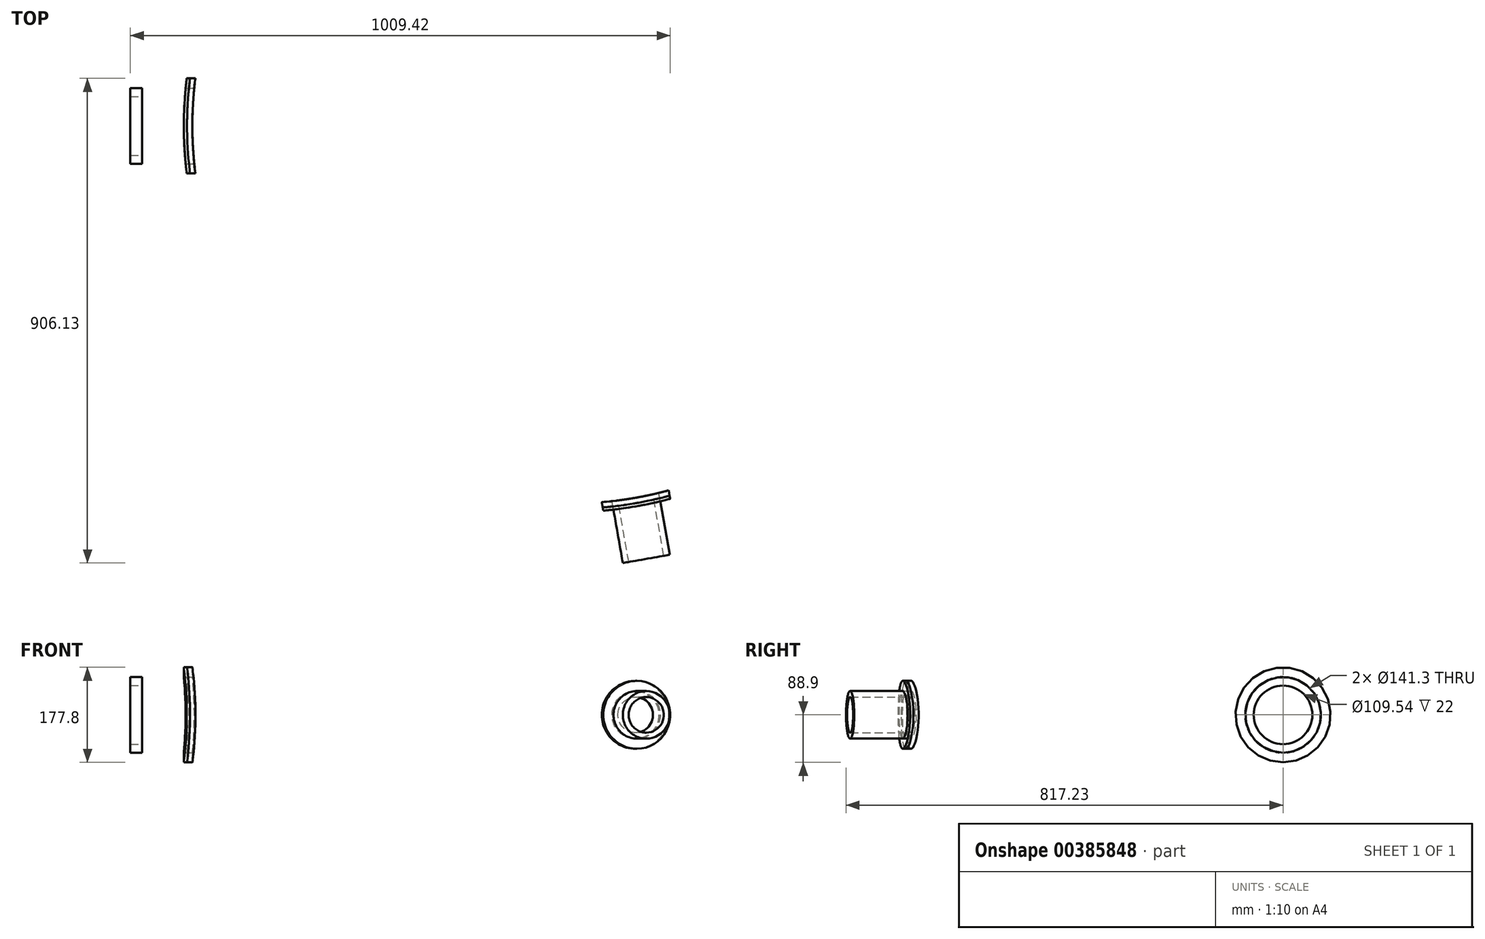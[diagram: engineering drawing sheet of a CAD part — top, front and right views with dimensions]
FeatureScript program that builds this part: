
annotation { "Feature Type Name" : "Feature", "Feature Type Description" : "" }
export const myFeature = defineFeature(function(context is Context, id is Id, definition is map)
    precondition{}
    {
        {
            var Q0;
            Q0=qCreatedBy(makeId("Top.planeOp"),FACE);
            var sketch = newSketch(context, id + "F0", { "sketchPlane" : qUnion([Q0])});
            skArc(sketch, "E0", {"start": v(-5.53, 715.98) * mm, "mid": v(-716, 0) * mm, "end": v(-5.53, -715.98) * mm});
            skArc(sketch, "E1.0", {"start": v(-1.5, 706) * mm, "mid": v(-706, 0) * mm, "end": v(-1.5, -706) * mm});
            skLineSegment(sketch, "E2", {"start": v(0, 716) * mm, "end": v(0, -716) * mm, "construction": true});
            skLineSegment(sketch, "E3", {"start": v(-716, 0) * mm, "end": v(716, 0) * mm, "construction": true});
            skLineSegment(sketch, "E4", {"start": v(1.5, 709) * mm, "end": v(1.5, 706) * mm});
            skCircle(sketch, "E5.0", {"center": v(0, 0) * mm, "radius": 709 * mm, "construction": true});
            skLineSegment(sketch, "E6", {"start": v(1.5, 709) * mm, "end": v(5.53, 715.98) * mm});
            skLineSegment(sketch, "E7.MirrorCS", {"start": v(-1.5, 709) * mm, "end": v(-1.5, 706) * mm});
            skLineSegment(sketch, "E8.MirrorCS", {"start": v(-1.5, 709) * mm, "end": v(-5.53, 715.98) * mm});
            skLineSegment(sketch, "E9.MirrorCS", {"start": v(1.5, -709) * mm, "end": v(1.5, -706) * mm});
            skLineSegment(sketch, "E10.MirrorCS", {"start": v(-1.5, -709) * mm, "end": v(-1.5, -706) * mm});
            skLineSegment(sketch, "E11.MirrorCS", {"start": v(-1.5, -709) * mm, "end": v(-5.53, -715.98) * mm});
            skLineSegment(sketch, "E12.MirrorCS", {"start": v(1.5, -709) * mm, "end": v(5.53, -715.98) * mm});
            skArc(sketch, "E13.trimOffspring", {"start": v(5.53, -715.98) * mm, "mid": v(716, 0) * mm, "end": v(5.53, 715.98) * mm});
            skArc(sketch, "E14.trimOffspring", {"start": v(1.5, -706) * mm, "mid": v(706, 0) * mm, "end": v(1.5, 706) * mm});
            skArc(sketch, "E15.0", {"start": v(-5.58, 721.98) * mm, "mid": v(-722, 0) * mm, "end": v(-5.58, -721.98) * mm});
            skLineSegment(sketch, "E16", {"start": v(-5.58, 721.98) * mm, "end": v(-5.53, 715.98) * mm});
            skLineSegment(sketch, "E17", {"start": v(-5.58, -721.98) * mm, "end": v(-5.53, -715.98) * mm});
            skLineSegment(sketch, "E18.MirrorCS", {"start": v(5.58, 721.98) * mm, "end": v(5.53, 715.98) * mm});
            skArc(sketch, "E19.MirrorCS", {"start": v(5.58, 721.98) * mm, "mid": v(722, 0) * mm, "end": v(5.58, -721.98) * mm});
            skLineSegment(sketch, "E20.MirrorCS", {"start": v(5.58, -721.98) * mm, "end": v(5.53, -715.98) * mm});
            skSolve(sketch);
        }
        {
            var Q0;
            Q0=makeQuery(id+"F0.imprint","IMPRINT",FACE,{"disambiguationData":[TD([[makeQuery(id+"F0.imprint","IMPRINT",EDGE,{"derivedFrom":sQuery(id+"F0.wireOp",EDGE,"E0")}),1.0]])]});
            var Q1;
            Q1=makeQuery(id+"F0.imprint","IMPRINT",FACE,{"disambiguationData":[TD([[makeQuery(id+"F0.imprint","IMPRINT",EDGE,{"derivedFrom":sQuery(id+"F0.wireOp",EDGE,"E4")}),1.0]])]});
            extrude(context, id + "F1", {"entities" : qUnion([Q0, Q1]), "endBound" : BoundingType.SYMMETRIC, "depth" : 1200 * mm});
        }
        {
            var Q0;
            Q0=qCreatedBy(makeId("Right.planeOp"),FACE);
            var sketch = newSketch(context, id + "F2", { "sketchPlane" : qUnion([Q0])});
            skLineSegment(sketch, "E21", {"start": v(0, 612.66) * mm, "end": v(0, -646.3) * mm, "construction": true});
            skLineSegment(sketch, "E22", {"start": v(-709, 600) * mm, "end": v(-726.72, 600) * mm});
            skLineSegment(sketch, "E23", {"start": v(-726.72, 600) * mm, "end": v(-726.72, 589.77) * mm});
            skLineSegment(sketch, "E24", {"start": v(-726.72, 589.77) * mm, "end": v(-709, 600) * mm});
            skLineSegment(sketch, "E25", {"start": v(-747.88, 0) * mm, "end": v(755.94, 0) * mm, "construction": true});
            skLineSegment(sketch, "E26.MirrorCS", {"start": v(-726.72, -600) * mm, "end": v(-726.72, -589.77) * mm});
            skLineSegment(sketch, "E27.MirrorCS", {"start": v(-709, -600) * mm, "end": v(-726.72, -600) * mm});
            skLineSegment(sketch, "E28.MirrorCS", {"start": v(-726.72, -589.77) * mm, "end": v(-709, -600) * mm});
            skSolve(sketch);
        }
        {
            var Q0;
            Q0 = qSketchRegion(id + "F2", true);
            var Q1;
            Q1=sQuery(id+"F2.wireOp",EDGE,"E21");
            revolve(context, id + "F3", {"operationType" : NewBodyOperationType.REMOVE, "entities" : qUnion([Q0]), "axis" : qUnion([Q1]), "revolveType" : RevolveType.FULL, "oppositeDirection" : true});
        }
        {
            var Q0;
            Q0 = qSketchRegion(id + "F2", true);
            var Q1;
            Q1=sQuery(id+"F2.wireOp",EDGE,"E21");
            revolve(context, id + "F4", {"operationType" : NewBodyOperationType.REMOVE, "entities" : qUnion([Q0]), "axis" : qUnion([Q1]), "revolveType" : RevolveType.FULL, "oppositeDirection" : true});
        }
        {
            var Q0;
            Q0=makeQuery(id+"F0.imprint","IMPRINT",FACE,{"disambiguationData":[TD([[makeQuery(id+"F0.imprint","IMPRINT",EDGE,{"derivedFrom":sQuery(id+"F0.wireOp",EDGE,"E0")}),-1.0]])]});
            extrude(context, id + "F5", {"entities" : qUnion([Q0]), "endBound" : BoundingType.SYMMETRIC, "depth" : 1200 * mm});
        }
        {
            var Q0;
            Q0=qCreatedBy(makeId("Right.planeOp"),FACE);
            var sketch = newSketch(context, id + "F6", { "sketchPlane" : qUnion([Q0])});
            skCircle(sketch, "E29", {"center": v(0, -450) * mm, "radius": 88.9 * mm});
            skLineSegment(sketch, "E30.bottom", {"start": v(-781.02, 685.97) * mm, "end": v(755.99, 685.97) * mm});
            skLineSegment(sketch, "E30.top", {"start": v(-781.02, -656.2) * mm, "end": v(755.99, -656.2) * mm});
            skLineSegment(sketch, "E30.left", {"start": v(-781.02, 685.97) * mm, "end": v(-781.02, -656.2) * mm});
            skLineSegment(sketch, "E30.right", {"start": v(755.99, 685.97) * mm, "end": v(755.99, -656.2) * mm});
            skSolve(sketch);
        }
        {
            var Q0;
            Q0=makeQuery(id+"F6.imprint","IMPRINT",FACE,{"disambiguationData":[TD([[makeQuery(id+"F6.imprint","IMPRINT",EDGE,{"derivedFrom":sQuery(id+"F6.wireOp",EDGE,"E29")}),-1.0]])]});
            extrude(context, id + "F7", {"entities" : qUnion([Q0]), "operationType" : NewBodyOperationType.REMOVE, "oppositeDirection" : true, "depth" : 1500 * mm});
        }
        {
            var Q0;
            Q0=qCreatedBy(makeId("Right.planeOp"),FACE);
            var sketch = newSketch(context, id + "F8", { "sketchPlane" : qUnion([Q0])});
            skCircle(sketch, "E31", {"center": v(0, -450) * mm, "radius": 70.65 * mm});
            skCircle(sketch, "E32.0", {"center": v(0, -450) * mm, "radius": 54.77 * mm});
            skSolve(sketch);
        }
        {
            var Q0;
            Q0=makeQuery(id+"F8.imprint","IMPRINT",FACE,{"disambiguationData":[TD([[makeQuery(id+"F8.imprint","IMPRINT",EDGE,{"derivedFrom":sQuery(id+"F8.wireOp",EDGE,"E32.0")}),1.0]])]});
            var Q1;
            Q1=makeQuery(id+"F8.imprint","IMPRINT",FACE,{"disambiguationData":[TD([[makeQuery(id+"F8.imprint","IMPRINT",EDGE,{"derivedFrom":sQuery(id+"F8.wireOp",EDGE,"E31")}),1.0]])]});
            extrude(context, id + "F9", {"entities" : qUnion([Q0, Q1]), "operationType" : NewBodyOperationType.REMOVE, "oppositeDirection" : true, "depth" : 1500 * mm});
        }
        {
            var Q0;
            Q0=makeQuery(id+"F8.imprint","IMPRINT",FACE,{"disambiguationData":[TD([[makeQuery(id+"F8.imprint","IMPRINT",EDGE,{"derivedFrom":sQuery(id+"F8.wireOp",EDGE,"E31")}),1.0]])]});
            extrude(context, id + "F10", {"entities" : qUnion([Q0]), "oppositeDirection" : true, "depth" : 822 * mm});
        }
        {
            var Q0;
            Q0=sQuery(id+"F2.wireOp",EDGE,"E21");
            cPlane(context, id + "F11", {"entities" : qUnion([Q0]), "cplaneType" : CPlaneType.LINE_ANGLE, "offset" : 25 * mm, "angle" : 80 * degree, "width" : 150 * mm, "height" : 150 * mm});
        }
        {
            var Q0;
            Q0=qCreatedBy(id+"F11.planeOp",FACE);
            var sketch = newSketch(context, id + "F12", { "sketchPlane" : qUnion([Q0])});
            skCircle(sketch, "E33", {"center": v(0, -450) * mm, "radius": 63.5 * mm});
            skCircle(sketch, "E34", {"center": v(0, -450) * mm, "radius": 44.45 * mm});
            skCircle(sketch, "E35.0", {"center": v(0, -450) * mm, "radius": 33.32 * mm});
            skLineSegment(sketch, "E36.bottom", {"start": v(-752.67, 633.78) * mm, "end": v(223.14, 633.78) * mm});
            skLineSegment(sketch, "E36.top", {"start": v(-752.67, -679.53) * mm, "end": v(223.14, -679.53) * mm});
            skLineSegment(sketch, "E36.left", {"start": v(-752.67, 633.78) * mm, "end": v(-752.67, -679.53) * mm});
            skLineSegment(sketch, "E36.right", {"start": v(223.14, 633.78) * mm, "end": v(223.14, -679.53) * mm});
            skSolve(sketch);
        }
        {
            var Q0;
            Q0=makeQuery(id+"F0.imprint","IMPRINT",FACE,{"disambiguationData":[TD([[makeQuery(id+"F0.imprint","IMPRINT",EDGE,{"derivedFrom":sQuery(id+"F0.wireOp",EDGE,"E13.trimOffspring")}),-1.0]])]});
            extrude(context, id + "F13", {"entities" : qUnion([Q0]), "endBound" : BoundingType.SYMMETRIC, "depth" : 1200 * mm});
        }
        {
            var Q0;
            Q0=makeQuery(id+"F12.imprint","IMPRINT",FACE,{"disambiguationData":[TD([[makeQuery(id+"F12.imprint","IMPRINT",EDGE,{"derivedFrom":sQuery(id+"F12.wireOp",EDGE,"E33")}),-1.0]])]});
            extrude(context, id + "F14", {"entities" : qUnion([Q0]), "operationType" : NewBodyOperationType.REMOVE, "endBound" : BoundingType.SYMMETRIC, "oppositeDirection" : true, "depth" : 1600 * mm});
        }
        {
            var Q0;
            Q0=makeQuery(id+"F12.imprint","IMPRINT",FACE,{"disambiguationData":[TD([[makeQuery(id+"F12.imprint","IMPRINT",EDGE,{"derivedFrom":sQuery(id+"F12.wireOp",EDGE,"E34")}),1.0]])]});
            var Q1;
            Q1=makeQuery(id+"F12.imprint","IMPRINT",FACE,{"disambiguationData":[TD([[makeQuery(id+"F12.imprint","IMPRINT",EDGE,{"derivedFrom":sQuery(id+"F12.wireOp",EDGE,"E35.0")}),1.0]])]});
            extrude(context, id + "F15", {"entities" : qUnion([Q0, Q1]), "operationType" : NewBodyOperationType.REMOVE, "oppositeDirection" : true, "depth" : 900 * mm});
        }
        {
            var Q0;
            Q0=makeQuery(id+"F12.imprint","IMPRINT",FACE,{"disambiguationData":[TD([[makeQuery(id+"F12.imprint","IMPRINT",EDGE,{"derivedFrom":sQuery(id+"F12.wireOp",EDGE,"E34")}),1.0]])]});
            var Q1;
            Q1=makeQuery(id+"F12.imprint","IMPRINT",FACE,{"disambiguationData":[TD([[makeQuery(id+"F12.imprint","IMPRINT",EDGE,{"derivedFrom":sQuery(id+"F12.wireOp",EDGE,"E35.0")}),1.0]])]});
            extrude(context, id + "F16", {"entities" : qUnion([Q0, Q1]), "operationType" : NewBodyOperationType.REMOVE, "oppositeDirection" : true, "depth" : 800 * mm});
        }
        {
            var Q0;
            Q0=makeQuery(id+"F12.imprint","IMPRINT",FACE,{"disambiguationData":[TD([[makeQuery(id+"F12.imprint","IMPRINT",EDGE,{"derivedFrom":sQuery(id+"F12.wireOp",EDGE,"E34")}),1.0]])]});
            extrude(context, id + "F17", {"entities" : qUnion([Q0]), "oppositeDirection" : true, "depth" : 822 * mm});
        }
        {
            var Q0;
            Q0=qCreatedBy(makeId("Top.planeOp"),FACE);
            var sketch = newSketch(context, id + "F18", { "sketchPlane" : qUnion([Q0])});
            skCircle(sketch, "E37", {"center": v(0, 0) * mm, "radius": 706 * mm});
            skSolve(sketch);
        }
        {
            var Q0;
            Q0=makeQuery(id+"F18.imprint","IMPRINT",FACE,{"disambiguationData":[TD([[makeQuery(id+"F18.imprint","IMPRINT",EDGE,{"derivedFrom":sQuery(id+"F18.wireOp",EDGE,"E37")}),1.0]])]});
            extrude(context, id + "F19", {"entities" : qUnion([Q0]), "operationType" : NewBodyOperationType.REMOVE, "oppositeDirection" : true, "depth" : 600 * mm});
        }
        {
            var Q0;
            Q0 = qSketchRegion(id + "F18", true);
            extrude(context, id + "F20", {"entities" : qUnion([Q0]), "operationType" : NewBodyOperationType.REMOVE, "oppositeDirection" : true, "depth" : 600 * mm});
        }
        {
            var Q0;
            Q0=makeQuery(id+"F8.imprint","IMPRINT",FACE,{"disambiguationData":[TD([[makeQuery(id+"F8.imprint","IMPRINT",EDGE,{"derivedFrom":sQuery(id+"F8.wireOp",EDGE,"E31")}),1.0]])]});
            var Q1;
            Q1=makeQuery(id+"F8.imprint","IMPRINT",FACE,{"disambiguationData":[TD([[makeQuery(id+"F8.imprint","IMPRINT",EDGE,{"derivedFrom":sQuery(id+"F8.wireOp",EDGE,"E32.0")}),1.0]])]});
            extrude(context, id + "F21", {"entities" : qUnion([Q0, Q1]), "operationType" : NewBodyOperationType.REMOVE, "oppositeDirection" : true, "depth" : 800 * mm});
        }
    });
